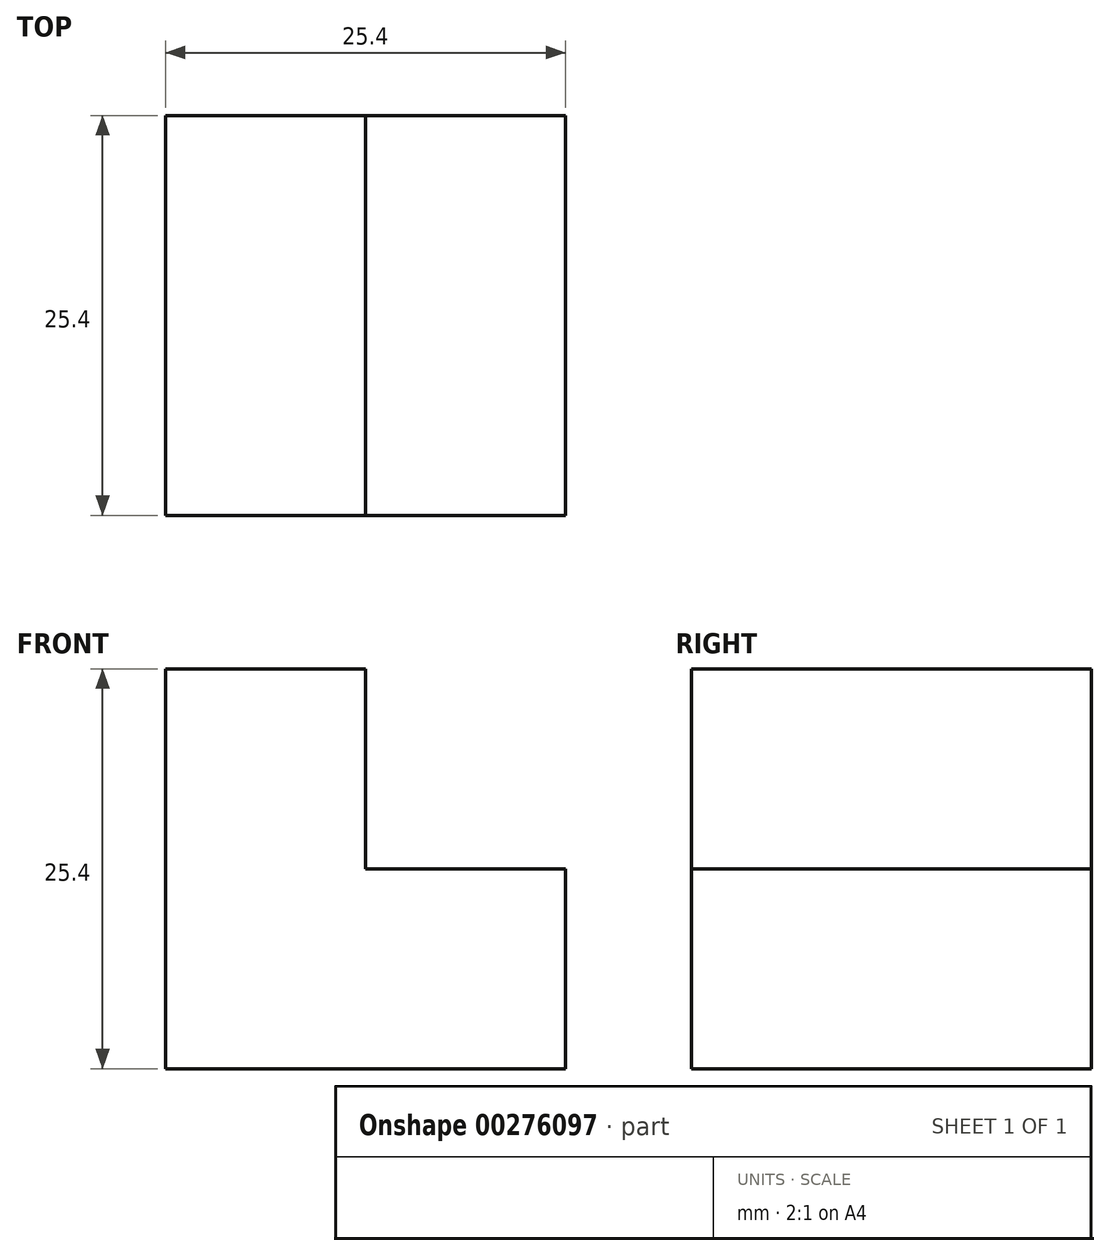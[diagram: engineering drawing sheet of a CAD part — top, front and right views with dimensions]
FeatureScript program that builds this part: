
annotation { "Feature Type Name" : "Feature", "Feature Type Description" : "" }
export const myFeature = defineFeature(function(context is Context, id is Id, definition is map)
    precondition{}
    {
        {
            var Q0;
            Q0=qCreatedBy(makeId("Front.planeOp"),FACE);
            var sketch = newSketch(context, id + "F0", { "sketchPlane" : qUnion([Q0])});
            skLineSegment(sketch, "E0", {"start": v(-27.88, 0) * mm, "end": v(-53.28, 0) * mm});
            skLineSegment(sketch, "E1", {"start": v(-53.28, 0) * mm, "end": v(-53.28, 25.4) * mm});
            skLineSegment(sketch, "E2", {"start": v(-53.28, 25.4) * mm, "end": v(-40.58, 25.4) * mm});
            skLineSegment(sketch, "E3", {"start": v(-40.58, 25.4) * mm, "end": v(-40.58, 12.7) * mm});
            skLineSegment(sketch, "E4", {"start": v(-40.58, 12.7) * mm, "end": v(-27.88, 12.7) * mm});
            skLineSegment(sketch, "E5", {"start": v(-27.88, 12.7) * mm, "end": v(-27.88, -1.72) * mm});
            skSolve(sketch);
        }
        {
            var Q0;
            Q0 = qSketchRegion(id + "F0", true);
            extrude(context, id + "F1", {"entities" : qUnion([Q0]), "depth" : 25.4 * mm});
        }
    });
